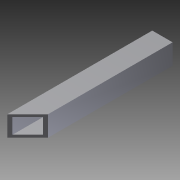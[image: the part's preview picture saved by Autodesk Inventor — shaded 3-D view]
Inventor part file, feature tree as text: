
AUTODESK INVENTOR PART (.ipt)
format: ipt  version: 2012 (Build 160160000, 160)  size: 88,576 bytes
history: native  units: in
note: dims shown in document units (in); Inventor stores cm internally (conversion verified against a paired STEP export)
features: extrude x2, sketch x2
ambient origin geometry x8: Origin, YZ Plane, XZ Plane, XY Plane, X Axis, Y Axis, Z Axis, Center Point
bodies: Solid1 (feature_tree)
feature tree (4):
  extrude  "Extrusion1"  Depth=1.0in
  extrude  "Extrusion3"  Depth=0.5in
  sketch  "Sketch1"  dims[d0=1.0in d1=1.0in]
  sketch  "Sketch3"  dims[d2=0.5in d3=0.5in d4=0.125in d5=0.125in d6=0.125in d7=0.125in d8=7.125in d9=0.0in d13=45.0deg d14=1.0in d15=0.0in]
